AUTODESK INVENTOR PART (.ipt)
format: ipt  version: 2017 (Build 210142000, 142)  size: 76,288 bytes
history: native  units: mm
features: reference x8, other x4, extrude x1, sketch x1
ambient origin geometry x8: Origin, YZ Plane, XZ Plane, XY Plane, X Axis, Y Axis, Z Axis, Center Point
bodies: Body1 (feature_tree)
feature tree (14):
  other  "Sólido1"
  extrude  "Extrusión1"  Depth=106.0mm
  sketch  "Boceto1"  dims[d0=15.0mm d1=106.0mm d2=6.0mm d3=0.0mm]
  reference  "Referencia1"
  reference  "Referencia2"
  reference  "Referencia3"
  reference  "Referencia4"
  reference  "Referencia5"
  reference  "Referencia6"
  reference  "Referencia7"
  reference  "Referencia8"
  other  "<userpath>\Documents\GitHub\actor-re-actor\models\inventor-caja\Case\Case-D.iam"
  other  "Case-D.iam"
  other  "Carcasa:1"
